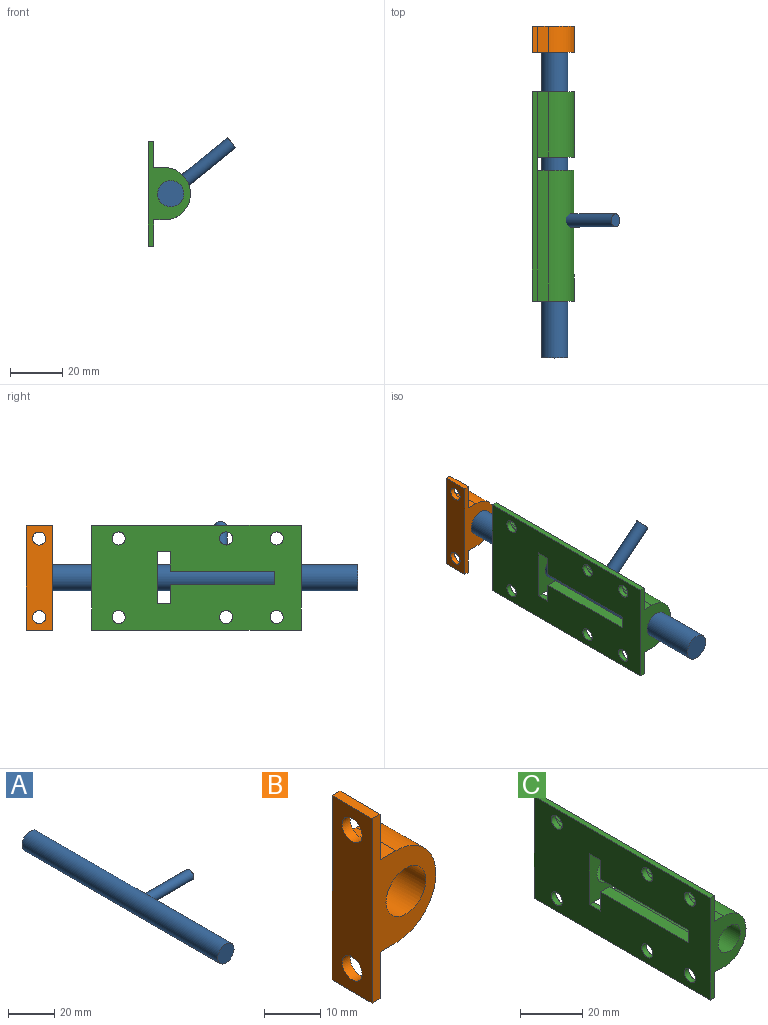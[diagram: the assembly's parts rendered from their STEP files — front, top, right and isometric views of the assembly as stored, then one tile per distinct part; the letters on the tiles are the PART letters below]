
ASSEMBLY  parts=3 mates=2
PART A: 5 faces, bbox 35.3x120x10 mm
  f0: cylinder r=2.5mm len=26.32mm, axis (-1,0,0), area 403.1mm2, adj f1,f2
  f1: plane 5x5mm, normal (1,0,0), area 19.6mm2, adj f0
  f2: cylinder r=5mm len=120mm, axis (0,1,0), area 3749.5mm2, adj f0,f3,f4
  f3: plane 10x10mm, normal (0,-1,0), area 78.5mm2, adj f2
  f4: plane 10x10mm, normal (0,1,0), area 78.5mm2, adj f2
PART B: 13 faces, bbox 16x10x40 mm
  f0: plane 40x16mm, normal (0,-1,0), area 238.5mm2, adj f1,f3,f4,f5,f6,f7,f8,f9
  f1: plane 10x4mm, normal (0,0,-1), area 40mm2, adj f0,f2,f6,f9
  f2: plane 40x16mm, normal (0,1,0), area 238.5mm2, adj f1,f3,f4,f5,f6,f7,f8,f9
  f3: plane 10x4mm, normal (0,0,1), area 40mm2, adj f0,f2,f8,f9
  f4: plane 10x2mm, normal (0,0,-1), area 20mm2, adj f0,f2,f5,f6
  f5: plane 40x10mm, normal (-1,0,0), area 360.7mm2, adj f0,f2,f4,f7,f11,f12
  f6: plane 10.06x10mm, normal (1,0,0), area 81mm2, adj f0,f1,f2,f4,f12
  f7: plane 10x2mm, normal (0,0,1), area 20mm2, adj f0,f2,f5,f8
  f8: plane 10x9.94mm, normal (1,0,0), area 79.7mm2, adj f0,f2,f3,f7,f11
  f9: cylinder r=10mm len=20mm, axis (0,1,0), area 314.2mm2, adj f0,f1,f2,f3
  f10: cylinder r=5mm len=10mm, axis (0,1,0), area 314.2mm2, adj f0,f2
  f11: cylinder r=2.5mm len=5mm, axis (1,0,0), area 31.4mm2, adj f5,f8
  f12: cylinder r=2.5mm len=5mm, axis (1,0,0), area 31.4mm2, adj f5,f6
PART C: 32 faces, bbox 16.1x80x40 mm
  f0: plane 5x2mm, normal (0,0,1), area 10mm2, adj f2,f12,f13,f19
  f1: plane 5x2mm, normal (0,0,-1), area 10mm2, adj f12,f15,f18,f19
  f2: plane 15.78x7.5mm, normal (0,1,0), area 84.2mm2, adj f0,f3,f12,f16,f17,f22,f24
  f3: plane 50x4.1mm, normal (0,0,-1), area 205mm2, adj f2,f7,f13,f16
  f4: plane 50x4.1mm, normal (0,0,1), area 205mm2, adj f7,f15,f16,f18
  f5: cylinder r=10mm len=25mm, axis (0,-1,0), area 785.4mm2, adj f8,f9,f10,f19
  f6: cylinder r=5mm len=25mm, axis (0,-1,0), area 785.4mm2, adj f9,f19
  f7: plane 40x16.1mm, normal (0,-1,0), area 240.5mm2, adj f3,f4,f11,f12,f13,f14,f15,f16
  f8: plane 25x4.1mm, normal (0,0,-1), area 102.5mm2, adj f5,f9,f13,f19
  f9: plane 40x16.1mm, normal (0,1,0), area 240.5mm2, adj f5,f6,f8,f10,f11,f12,f13,f14
  f10: plane 25x4.1mm, normal (0,0,1), area 102.5mm2, adj f5,f9,f15,f19
  f11: plane 80x2mm, normal (0,0,-1), area 160mm2, adj f7,f9,f12,f13
  f12: plane 80x40mm, normal (-1,0,0), area 2782.2mm2, adj f0,f1,f2,f7,f9,f11,f14,f18
  f13: plane 80x10mm, normal (1,0,0), area 741.1mm2, adj f0,f3,f7,f8,f9,f11,f29,f30
  f14: plane 80x2mm, normal (0,0,1), area 160mm2, adj f7,f9,f12,f15
  f15: plane 80x10mm, normal (1,0,0), area 741.1mm2, adj f1,f4,f7,f9,f10,f14,f26,f27
  f16: cylinder r=10mm len=50mm, axis (0,-1,0), area 1368.7mm2, adj f2,f3,f4,f7,f18,f23,f24,f25
  f17: cylinder r=5mm len=50mm, axis (0,-1,0), area 1151.9mm2, adj f2,f7,f18,f20,f21,f22,f23,f24
  f18: plane 15.78x7.5mm, normal (0,1,0), area 84.2mm2, adj f1,f4,f12,f16,f17,f20,f25
  f19: plane 20x16.1mm, normal (0,-1,0), area 200.5mm2, adj f0,f1,f5,f6,f8,f10,f12
  f20: plane 40x4.22mm, normal (0,0,-1), area 168.8mm2, adj f12,f17,f18,f21
  f21: plane 5x4.22mm, normal (0,1,0), area 18.8mm2, adj f12,f17,f20,f22
  f22: plane 40x4.22mm, normal (0,0,1), area 168.8mm2, adj f2,f12,f17,f21
  f23: plane 5x3.22mm, normal (0,1,0), area 13.3mm2, adj f16,f17,f24,f25
  f24: plane 40x2.9mm, normal (0,0,1), area 116.1mm2, adj f2,f16,f17,f23
  f25: plane 40x2.9mm, normal (0,0,-1), area 116.1mm2, adj f16,f17,f18,f23
  f26: cylinder r=2.5mm len=5mm, axis (1,0,0), area 31.4mm2, adj f12,f15
  f27: cylinder r=2.5mm len=5mm, axis (1,0,0), area 31.4mm2, adj f12,f15
  f28: cylinder r=2.5mm len=5mm, axis (1,0,0), area 31.4mm2, adj f12,f15
  f29: cylinder r=2.5mm len=5mm, axis (1,0,0), area 31.4mm2, adj f12,f13
  f30: cylinder r=2.5mm len=5mm, axis (1,0,0), area 31.4mm2, adj f12,f13
  f31: cylinder r=2.5mm len=5mm, axis (1,0,0), area 31.4mm2, adj f12,f13
PLACE A rot(axis=(0,-1,0),39deg) t=(-13.5,-71.68,19.71)mm
PLACE B t=(-5.05,-46.52,-20.06)mm
PLACE C t=(-5.1,-50,-20)mm
MATE fastened C.f6 <-> B.f10  axis (0,-1,0) through (2.45,30,0)mm
MATE cylindrical A.f2 <-> C.f6  axis (0,1,0) through (2.45,48.32,0)mm
